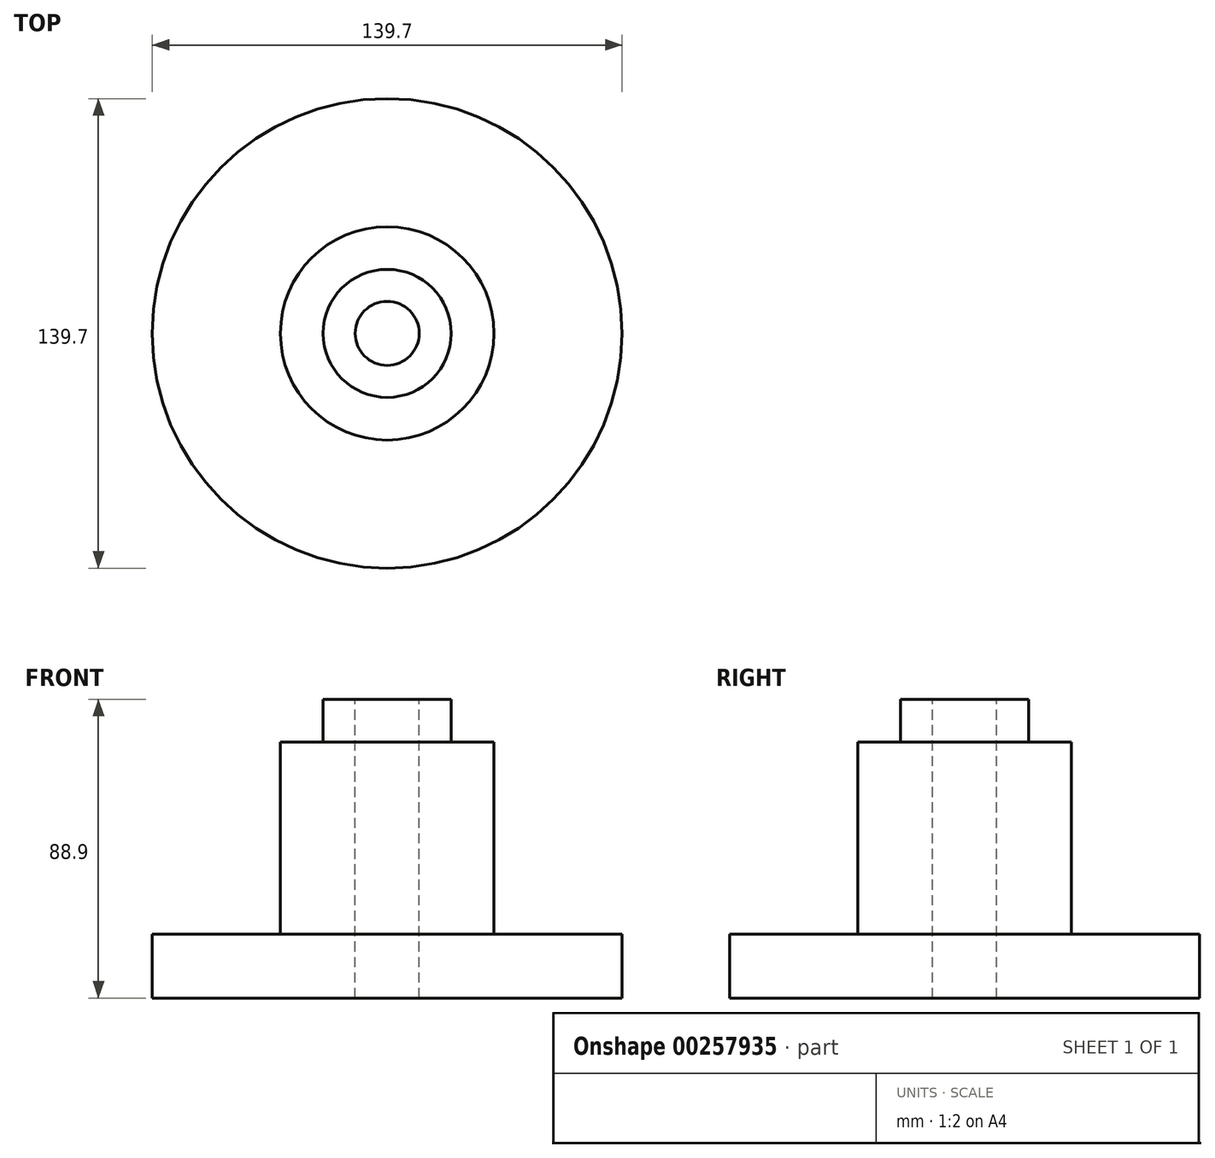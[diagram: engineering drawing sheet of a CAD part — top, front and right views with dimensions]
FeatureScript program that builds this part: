
annotation { "Feature Type Name" : "Feature", "Feature Type Description" : "" }
export const myFeature = defineFeature(function(context is Context, id is Id, definition is map)
    precondition{}
    {
        {
            var Q0;
            Q0=qCreatedBy(makeId("Front.planeOp"),FACE);
            var sketch = newSketch(context, id + "F0", { "sketchPlane" : qUnion([Q0])});
            skLineSegment(sketch, "E0", {"start": v(0, 0) * mm, "end": v(0, 88.9) * mm});
            skLineSegment(sketch, "E1", {"start": v(0, 88.9) * mm, "end": v(19.05, 88.9) * mm});
            skLineSegment(sketch, "E2", {"start": v(19.05, 88.9) * mm, "end": v(19.05, 76.2) * mm});
            skLineSegment(sketch, "E3", {"start": v(19.05, 76.2) * mm, "end": v(31.75, 76.2) * mm});
            skLineSegment(sketch, "E4", {"start": v(31.75, 76.2) * mm, "end": v(31.75, 19.05) * mm});
            skLineSegment(sketch, "E5", {"start": v(31.75, 19.05) * mm, "end": v(69.85, 19.05) * mm});
            skLineSegment(sketch, "E6", {"start": v(69.85, 19.05) * mm, "end": v(69.85, 0) * mm});
            skLineSegment(sketch, "E7", {"start": v(69.85, 0) * mm, "end": v(0, 0) * mm});
            skSolve(sketch);
        }
        {
            var Q0;
            Q0 = qSketchRegion(id + "F0", true);
            var Q1;
            Q1=sQuery(id+"F0.wireOp",EDGE,"E0");
            revolve(context, id + "F1", {"entities" : qUnion([Q0]), "axis" : qUnion([Q1]), "revolveType" : RevolveType.FULL});
        }
        {
            var Q0;
            Q0=makeQuery(id+"F1.opRevolve","SWEPT_FACE",FACE,{"disambiguationData":[OSD([sQuery(id+"F0.wireOp",EDGE,"E1")])]});
            var sketch = newSketch(context, id + "F2", { "sketchPlane" : qUnion([Q0])});
            skCircle(sketch, "E8", {"center": v(0, 0) * mm, "radius": 9.53 * mm});
            skSolve(sketch);
        }
        {
            var Q0;
            Q0=sQuery(id+"F2.wireOp",VERTEX,"E8.center");
            var Q1;
            Q1=makeQuery(id+"F1.opRevolve","SWEPT_BODY",BODY,{"disambiguationData":[OSD([sQuery(id+"F0.wireOp",EDGE,"E0"),sQuery(id+"F0.wireOp",EDGE,"E1"),sQuery(id+"F0.wireOp",EDGE,"E2"),sQuery(id+"F0.wireOp",EDGE,"E3"),sQuery(id+"F0.wireOp",EDGE,"E4"),sQuery(id+"F0.wireOp",EDGE,"E5"),sQuery(id+"F0.wireOp",EDGE,"E6"),sQuery(id+"F0.wireOp",EDGE,"E7")])]});
            hole(context, id + "F3", {"style" : HoleStyle.SIMPLE, "endStyle" : HoleEndStyle.THROUGH, "holeDiameter" : 19.05 * mm, "tappedDepth" : 12.7 * mm, "tapClearance" : 3, "locations" : qUnion([Q0]), "scope" : qUnion([Q1])});
        }
    });
